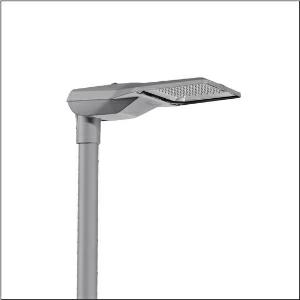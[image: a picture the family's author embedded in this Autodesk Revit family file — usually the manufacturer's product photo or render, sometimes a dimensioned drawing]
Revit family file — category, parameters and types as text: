
# Revit family: streetlight_sl_21_midi___st0_8a_5xe3c43s08mb_603c
name_source: partatom
category: Lighting Fixtures
units: mm (PartAtom-declared; Revit-internal decimal feet)

## family parameters
Cut with Voids When Loaded = No
Host = Face
Light Source = No
Part Type = Normal
Room Calculation Point = No
Round Connector Dimension = Use Diameter
Shared = No

## types (1)
- --- (1 x LED, 20180 lm, 147 W, 4000K)
    Apparent Load = 147 VA
    CIE Flux Codes = 38 75 97 100 100
    Color Rendering = 70
    Color Temperature = 4000K
    Default Elevation = 1800 mm
    Description = Streetlight SL 21 midi, mast luminaire, primary light control with lens, of PMMA, primary optical cover: cover, of toughened safety glass, transparent, light distribution: ST0.8a, light emission: direct distribution, primary light characteristic: asymmetric, installation type: side-entry, post-top, LED, High Power LED, rated luminous flux: 20.180lm, luminous efficacy: 137lm/W, light colour: 740, colour temperature: 4000K, control: overheat protection, constant luminous flux control, time-dependent luminous flux control, flexible luminous flux parameterisation, presetting dimming logarithmic, mains connection: 230..240V, AC, 50/60Hz, start of lifetime: 147W, end of service life: 155W, reduction: 65W, luminaire housing, of diecast aluminium, powder-coated, Siteco® metallic grey (DB 702S), corrosivity category C5 mid according to DIN EN ISO 12944, please order mast flange separately, inclination adjustable: 0°, 5°, 10°, 15°, sealing non-destructively replaceable, multi-level sealing system, length: 644mm, width: 335mm, height: 110mm, mast flange for spigot size: 42mm (side-entry): 5XC10008XM4, 60/48mm (side-entry/post-top): 5XC10108XM2, 76/60mm (side-entry/post-top): 5XC10108XM1, Smart Interface above, protection rating (complete): IP66, insulation class (complete): insulation class II (safety insulation), certification: CE, ENEC, ENEC+, VDE, impact resistance: IK09, permissible operating ambient temperature for outdoor applications: -40..+50°C, standard-compliant lighting for roads and squares, packaging unit: 1 piece

Light Distribution: ST0.8a
    Height = 111 mm
    Lamp = 1 x LED
    Lamp Light Flux = 20180 lm
    Lamp Power = 147 W
    Lamp count = 1
    Length = 644 mm
    Luminous efficacy = 137 lm/W
    Manufacturer = Siteco
    ModVariant = No
    Model = 5XE3C43S08MB
    Number of Poles = 1
    OnlyDefault = Yes
    Power Factor = 1
    Product Name = Streetlight SL 21 midi | ST0.8a
    Product group = mast luminaire | pylon top
    ProductGroupID = 6100
    Protection Class = Protection class II
    Protection Degree = IP 66
    RLX_Detail_Level = 1
    RLX_Emergency_Light_Flux = 0 lm
    RLX_Emergency_Type = 0
    RLX_Emergency_Type_DB = No
    RlxData = <blob elided: 91109 chars, md5=18c47e41>
    Socket = socket
    Standby Power = 0 W
    System Light Flux = 20180 lm
    System Power = 147 W
    Type Comments = factory setting: luminous flux: 100 % | dim-lin: 254 | 750 mA
    Type Image = l_1004302.jpg
    URL = http://relux.com
    VarID = @adj_137821
    Voltage = 0 V
    Weight = 0.00 kg
    Width = 336 mm

## geometry (parser evidence)
native form markers: Blend x4, Sweep x11
no freeform markers — native parametric forms only
